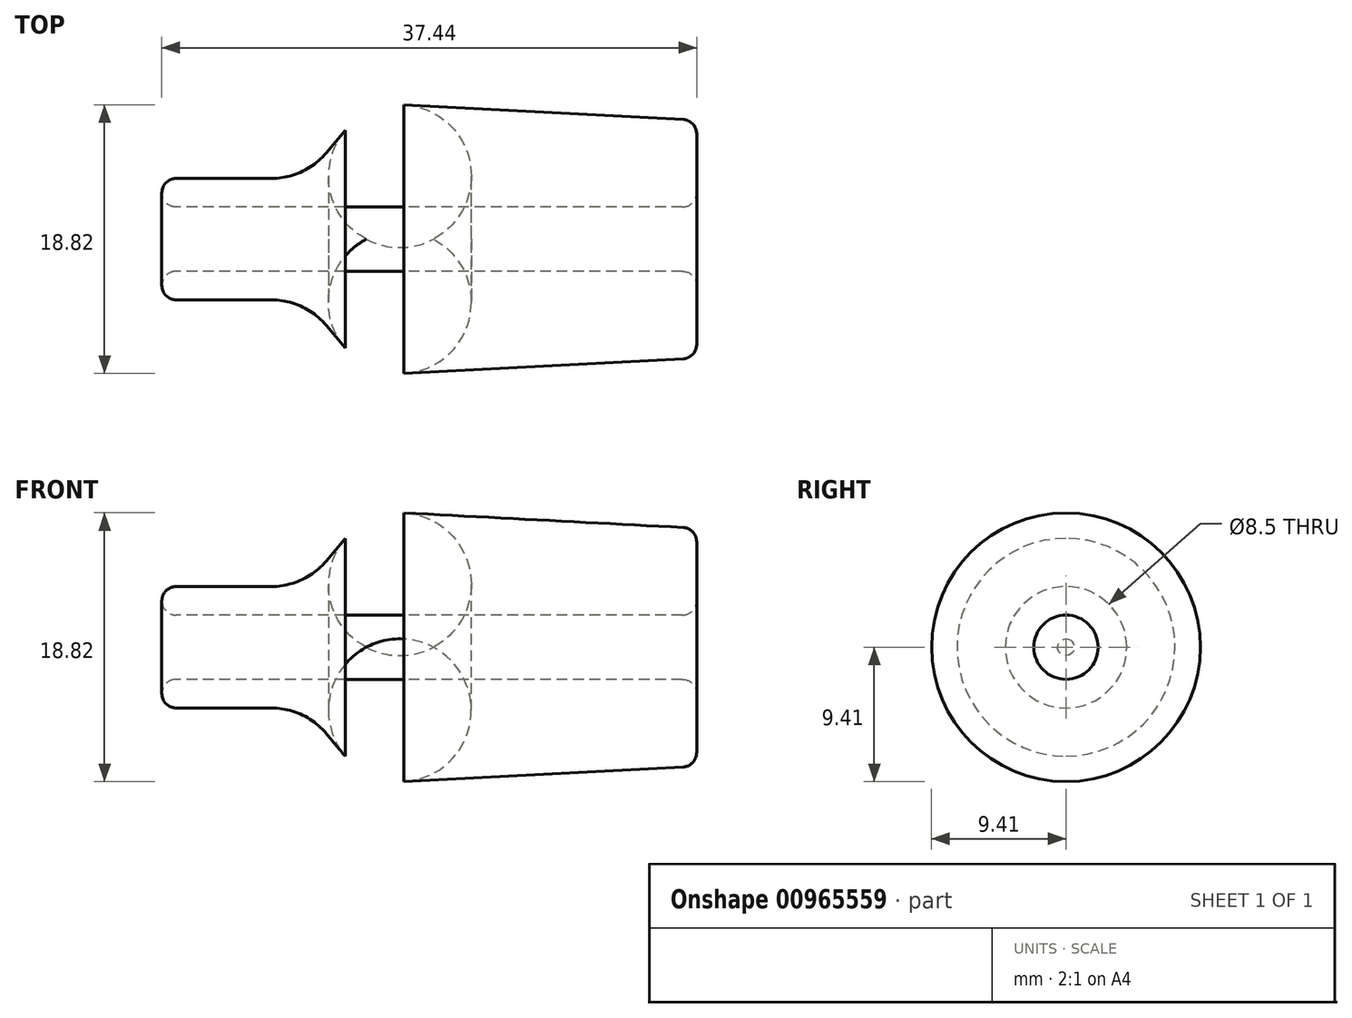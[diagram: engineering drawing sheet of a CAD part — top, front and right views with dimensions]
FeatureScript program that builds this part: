
annotation { "Feature Type Name" : "Feature", "Feature Type Description" : "" }
export const myFeature = defineFeature(function(context is Context, id is Id, definition is map)
    precondition{}
    {
        {
            var Q0;
            Q0=qCreatedBy(makeId("Front.planeOp"),FACE);
            var sketch = newSketch(context, id + "F0", { "sketchPlane" : qUnion([Q0])});
            skLineSegment(sketch, "E0", {"start": v(-80, 0) * mm, "end": v(0, 0) * mm, "construction": true});
            skLineSegment(sketch, "E1", {"start": v(0, 2.25) * mm, "end": v(0, 4.25) * mm});
            skLineSegment(sketch, "E2", {"start": v(0, 4.25) * mm, "end": v(10, 4.25) * mm});
            skLineSegment(sketch, "E3", {"start": v(10, 4.25) * mm, "end": v(14.44, 9.54) * mm});
            skLineSegment(sketch, "E4", {"start": v(14.44, 9.54) * mm, "end": v(37.44, 8.33) * mm});
            skLineSegment(sketch, "E5.bottom", {"start": v(29.44, 8.75) * mm, "end": v(45.44, 8.75) * mm, "construction": true});
            skLineSegment(sketch, "E5.top", {"start": v(29.44, -8.75) * mm, "end": v(45.44, -8.75) * mm, "construction": true});
            skLineSegment(sketch, "E5.left", {"start": v(29.44, 8.75) * mm, "end": v(29.44, -8.75) * mm, "construction": true});
            skLineSegment(sketch, "E5.right", {"start": v(45.44, 8.75) * mm, "end": v(45.44, -8.75) * mm, "construction": true});
            skPoint(sketch, "E5.middle", {"position": v(37.44, 0) * mm});
            skLineSegment(sketch, "E6", {"start": v(0, 2.25) * mm, "end": v(14.44, 2.25) * mm});
            skLineSegment(sketch, "E7", {"start": v(14.44, 2.25) * mm, "end": v(37.44, 2.25) * mm});
            skLineSegment(sketch, "E8", {"start": v(37.44, 2.25) * mm, "end": v(37.44, 8.33) * mm});
            skSolve(sketch);
        }
        {
            var Q0;
            Q0 = qSketchRegion(id + "F0", true);
            var Q1;
            Q1=sQuery(id+"F0.wireOp",EDGE,"E0");
            revolve(context, id + "F1", {"surfaceOperationType" : NewSurfaceOperationType.NEW, "entities" : qUnion([Q0]), "axis" : qUnion([Q1]), "revolveType" : RevolveType.FULL});
        }
        {
            var Q0;
            Q0=makeQuery(id+"F1.opRevolve","SWEPT_EDGE",EDGE,{"disambiguationData":[OSD([sQuery(id+"F0.wireOp",EDGE,"E1"),sQuery(id+"F0.wireOp",EDGE,"E2")])]});
            var Q1;
            Q1=makeQuery(id+"F1.opRevolve","SWEPT_EDGE",EDGE,{"disambiguationData":[OSD([sQuery(id+"F0.wireOp",EDGE,"E4"),sQuery(id+"F0.wireOp",EDGE,"E8")])]});
            var Q2;
            Q2=makeQuery(id+"F1.opRevolve","SWEPT_EDGE",EDGE,{"disambiguationData":[OSD([sQuery(id+"F0.wireOp",EDGE,"E7"),sQuery(id+"F0.wireOp",EDGE,"E8")])]});
            var Q3;
            Q3=makeQuery(id+"F1.opRevolve","SWEPT_EDGE",EDGE,{"disambiguationData":[OSD([sQuery(id+"F0.wireOp",EDGE,"E1"),sQuery(id+"F0.wireOp",EDGE,"E6")])]});
            fillet(context, id + "F2", {"entities" : qUnion([Q0, Q1, Q2, Q3]), "radius" : 1 * mm, "tangentPropagation" : true, "allowEdgeOverflow" : false});
        }
        {
            var Q0;
            Q0=makeQuery(id+"F1.opRevolve","SWEPT_EDGE",EDGE,{"disambiguationData":[OSD([sQuery(id+"F0.wireOp",EDGE,"E3"),sQuery(id+"F0.wireOp",EDGE,"E4")])]});
            var Q1;
            Q1=makeQuery(id+"F1.opRevolve","SWEPT_EDGE",EDGE,{"disambiguationData":[OSD([sQuery(id+"F0.wireOp",EDGE,"E2"),sQuery(id+"F0.wireOp",EDGE,"E3")])]});
            fillet(context, id + "F3", {"entities" : qUnion([Q0, Q1]), "radius" : 5 * mm, "tangentPropagation" : true, "allowEdgeOverflow" : false});
        }
    });
